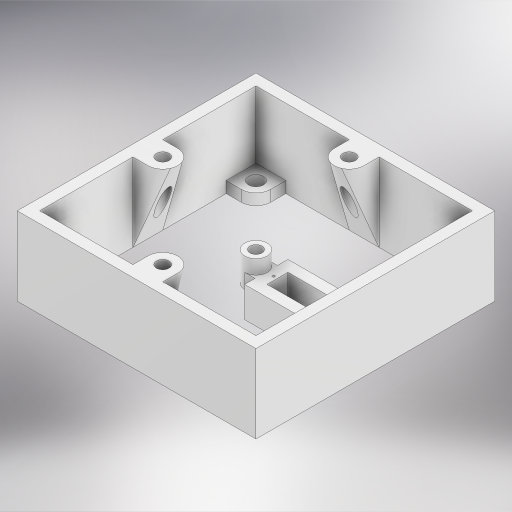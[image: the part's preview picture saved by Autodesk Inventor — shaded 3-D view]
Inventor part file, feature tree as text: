
AUTODESK INVENTOR PART (.ipt)
format: ipt  version: 2024 (Build 280153000, 153)  size: 540,160 bytes
history: native  units: in
note: dims shown in document units (in); Inventor stores cm internally (conversion verified against a paired STEP export)
features: sketch x8, extrude x5, pattern_circular x2, other x2, hole x2, plane x2, projected_geometry x2, chamfer x1, loft x1
ambient origin geometry x8: Origin, YZ Plane, XZ Plane, XY Plane, X Axis, Y Axis, Z Axis, Center Point
bodies: Body1 (feature_tree)
feature tree (25):
  extrude  "Extrusion3"  Depth=4.0in
  extrude  "Extrusion4"  Depth=1.3125in TaperAngle=0.0deg
  pattern_circular  "Circular Pattern1"  Count=4 Angle=360.0deg
  extrude  "Extrusion5"  Depth=0.1378in
  chamfer  "Chamfer1"  Distance=0.7874in
  other  "Work Axis1"
  extrude  "Extrusion9"  Depth=3.625in
  extrude  "Extrusion10"  Depth=0.5118in TaperAngle=0.0deg
  other  "Work Point1"
  hole  "Hole1"  [1 undecoded]
  loft  "Loft1"
  hole  "Hole2"  [1 undecoded]
  pattern_circular  "Circular Pattern2"  [2 undecoded]
  sketch  "Sketch3"  dims[d17=4.0in d18=4.0in]
  sketch  "Sketch4"  dims[d19=0.1875in d20=1.3125in d21=0.0in]
  sketch  "Sketch5"  dims[d22=4.0in]
  plane  "Work Plane2"
  plane  "Work Plane3"
  sketch  "Sketch9"  dims[d23=4.0in]
  sketch  "Sketch10"  dims[d24=0.1875in]
  sketch  "Sketch11"  dims[d25=0.25in]
  projected_geometry  "Projected Loop3"
  sketch  "Sketch12"  dims[d26=0.125in]
  sketch  "Sketch13"  dims[d27=0.1875in d28=0.0in d30=1.5748in d31=360.0deg d33=0.1378in d34=0.7874in d35=3.625in d36=0.5118in d37=0.0in d38=0.0079in d39=0.1875in d69=0.375in d70=0.125in d71=45.0deg d72=1.0in d73=0.1555in d74=0.3346in d75=0.25in d76=0.0394in d77=0.1225in d78=0.7874in d80=180.0deg d82=0.375in d83=0.375in d84=0.25in d85=0.0in d86=0.375in d87=0.2382in d88=0.0in d89=1.0in d90=1.0in d91=0.201in d92=0.75in d93=0.375in d94=0.25in d95=0.5635in d96=1.0in d97=0.8108in d98=0.5in d99=0.5in d100=0.25in d101=0.0in d102=90.0deg d103=0.0in d104=90.0deg d105=0.21in d106=0.75in d107=0.375in d108=0.25in d109=0.5635in d110=1.0in d111=0.8108in d112=1.1811in d113=180.0deg d16=0.0312in]
  projected_geometry  "Projected Loop5"
note: 4 required parameter values undecoded (feature->parameter linkage not recoverable at this tier; creation-order binding heuristic only, values carry confidence <= 0.55)
